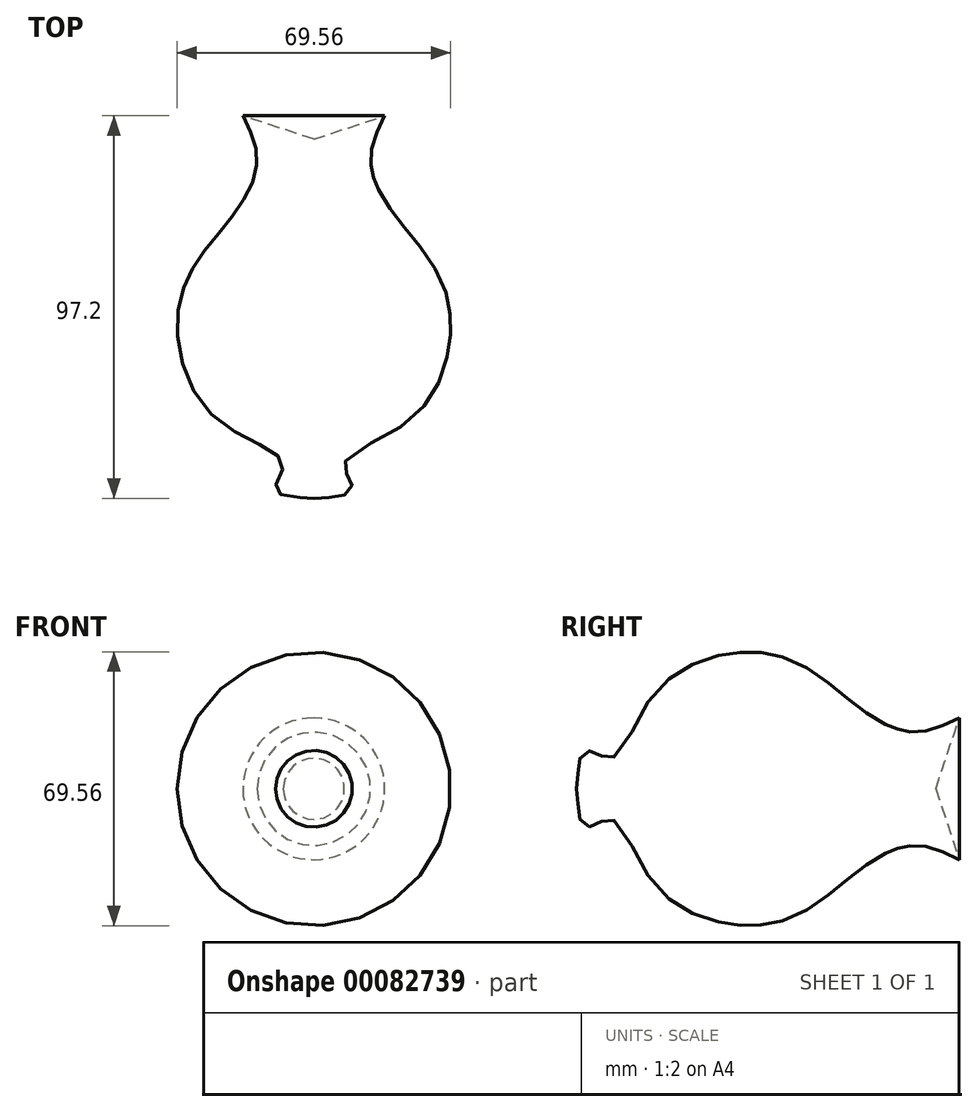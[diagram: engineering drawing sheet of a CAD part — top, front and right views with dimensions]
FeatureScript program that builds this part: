
annotation { "Feature Type Name" : "Feature", "Feature Type Description" : "" }
export const myFeature = defineFeature(function(context is Context, id is Id, definition is map)
    precondition{}
    {
        {
            var Q0;
            Q0=qCreatedBy(makeId("Top.planeOp"),FACE);
            var sketch = newSketch(context, id + "F0", { "sketchPlane" : qUnion([Q0])});
            skLineSegment(sketch, "E0", {"start": v(0, 45.5) * mm, "end": v(-18.02, 51.43) * mm});
            skFitSpline(sketch, "E1", {"points": [v(-18.02, 51.43) * mm, v(-14.43, 41.08) * mm, v(-18.02, 29.75) * mm, v(-28.23, 16.5) * mm, v(-34.72, 0) * mm, v(-24.65, -25.75) * mm, v(-7.8, -37.2) * mm, v(-9.46, -44.11) * mm, v(0, -45.77) * mm, v(0, -45.9) * mm], "startDerivative": vector(47.68, -95.36) * mm, "endDerivative": vector(-8.25, -12.37) * mm});
            skLineSegment(sketch, "E2", {"start": v(0, 45.5) * mm, "end": v(0, -45.77) * mm});
            skSolve(sketch);
        }
        {
            var Q0;
            {var subQ0=sQuery(id+"F0.wireOp",EDGE,"E0");Q0=makeQuery(id+"F0.imprint","IMPRINT",FACE,{"disambiguationData":[TD([[makeQuery(id+"F0.imprint","IMPRINT",EDGE,{"derivedFrom":subQ0}),1.0]])]});}
            var Q1;
            Q1=sQuery(id+"F0.wireOp",EDGE,"E2");
            revolve(context, id + "F1", {"entities" : qUnion([Q0]), "axis" : qUnion([Q1]), "revolveType" : RevolveType.FULL});
        }
    });
